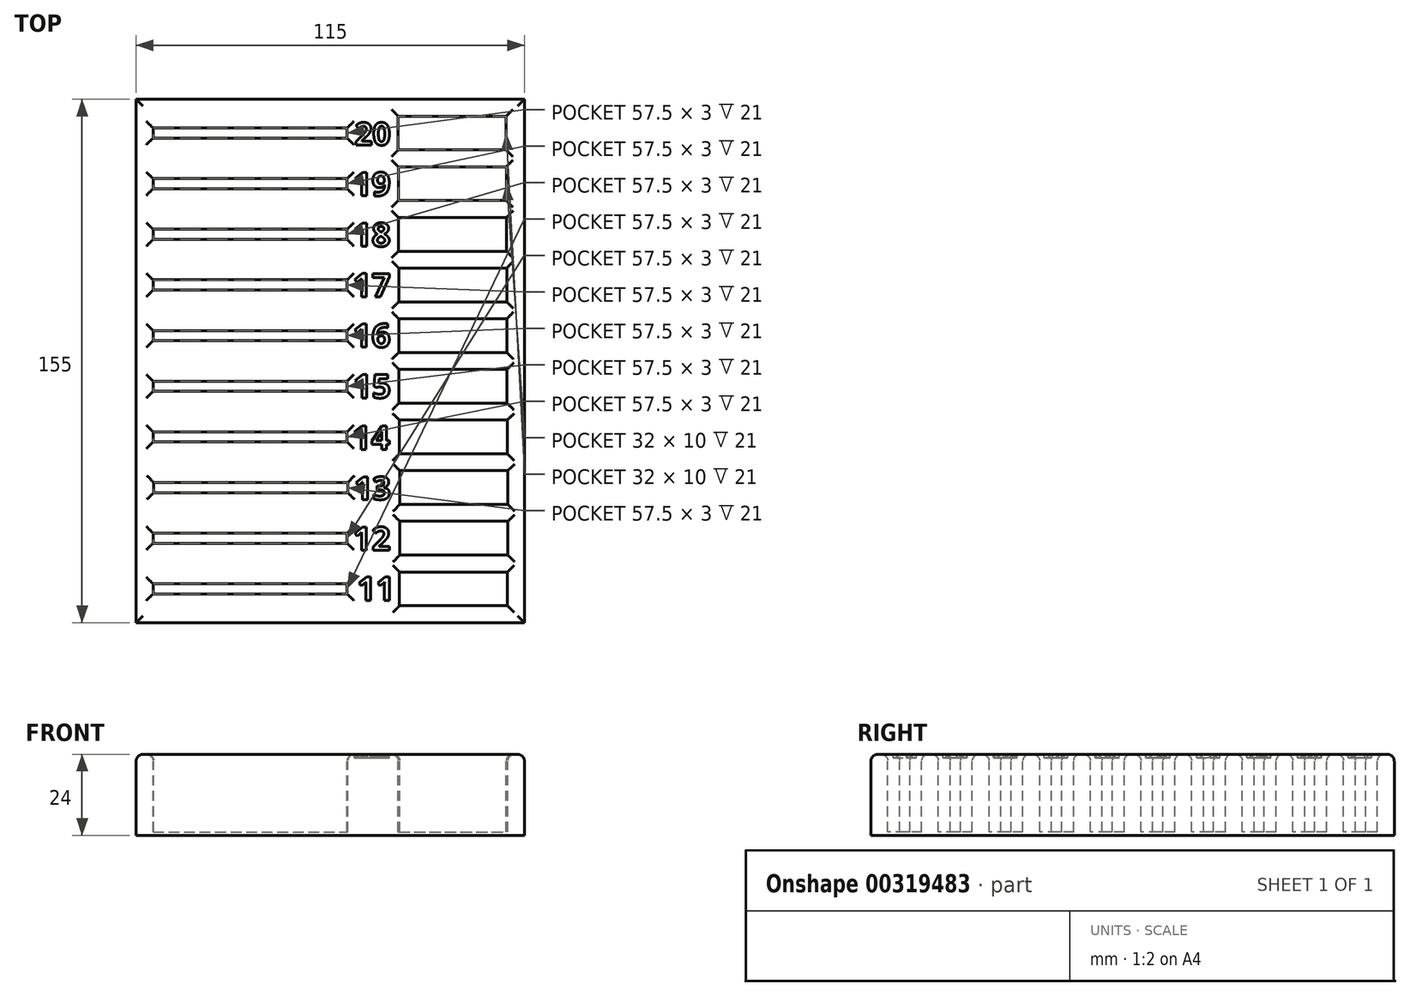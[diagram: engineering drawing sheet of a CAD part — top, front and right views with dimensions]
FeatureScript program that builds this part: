
annotation { "Feature Type Name" : "Feature", "Feature Type Description" : "" }
export const myFeature = defineFeature(function(context is Context, id is Id, definition is map)
    precondition{}
    {
        {
            var Q0;
            Q0=qCreatedBy(makeId("Top.planeOp"),FACE);
            var sketch = newSketch(context, id + "F0", { "sketchPlane" : qUnion([Q0])});
            skLineSegment(sketch, "E0.bottom", {"start": v(-49.85, 126.63) * mm, "end": v(65.15, 126.63) * mm});
            skLineSegment(sketch, "E0.top", {"start": v(-49.85, -28.37) * mm, "end": v(65.15, -28.37) * mm});
            skLineSegment(sketch, "E0.left", {"start": v(-49.85, 126.63) * mm, "end": v(-49.85, -28.37) * mm});
            skLineSegment(sketch, "E0.right", {"start": v(65.15, 126.63) * mm, "end": v(65.15, -28.37) * mm});
            skSolve(sketch);
        }
        {
            var Q0;
            Q0=makeQuery(id+"F0.imprint","IMPRINT",FACE,{"disambiguationData":[TD([[makeQuery(id+"F0.imprint","IMPRINT",EDGE,{"derivedFrom":sQuery(id+"F0.wireOp",EDGE,"E0.bottom")}),-1.0]])]});
            var Q1;
            Q1=makeQuery(id+"F0.imprint","IMPRINT",FACE,{"disambiguationData":[TD([[makeQuery(id+"F0.imprint","IMPRINT",EDGE,{"derivedFrom":sQuery(id+"F0.wireOp",EDGE,"eXpO4zti-W6eb-gkUP-Bc0d-zbJJjk6ygzeg.bottom")}),-1.0]])]});
            var Q2;
            Q2=makeQuery(id+"F0.imprint","IMPRINT",FACE,{"disambiguationData":[TD([[makeQuery(id+"F0.imprint","IMPRINT",EDGE,{"derivedFrom":sQuery(id+"F0.wireOp",EDGE,"IiJkesfC-iyIp-GpGT-9vFS-BzQ84R5pHUzr.bottom")}),-1.0]])]});
            extrude(context, id + "F1", {"entities" : qUnion([Q0, Q1, Q2]), "depth" : 24 * mm});
        }
        {
            var Q0;
            Q0=makeQuery(id+"F1.opExtrude","CAP_FACE",FACE,{"disambiguationData":[OSD([sQuery(id+"F0.wireOp",EDGE,"E0.bottom"),sQuery(id+"F0.wireOp",EDGE,"E0.top"),sQuery(id+"F0.wireOp",EDGE,"E0.left"),sQuery(id+"F0.wireOp",EDGE,"E0.right")])],"isStart":false});
            var sketch = newSketch(context, id + "F2", { "sketchPlane" : qUnion([Q0])});
            skLineSegment(sketch, "E1.bottom", {"start": v(-44.85, -16.87) * mm, "end": v(12.65, -16.87) * mm});
            skLineSegment(sketch, "E1.top", {"start": v(-44.85, -19.87) * mm, "end": v(12.65, -19.87) * mm});
            skLineSegment(sketch, "E1.left", {"start": v(-44.85, -16.87) * mm, "end": v(-44.85, -19.87) * mm});
            skLineSegment(sketch, "E1.right", {"start": v(12.65, -16.87) * mm, "end": v(12.65, -19.87) * mm});
            skLineSegment(sketch, "E2.bottom", {"start": v(28.15, -13.37) * mm, "end": v(60.15, -13.37) * mm});
            skLineSegment(sketch, "E2.top", {"start": v(28.15, -23.37) * mm, "end": v(60.15, -23.37) * mm});
            skLineSegment(sketch, "E2.left", {"start": v(28.15, -13.37) * mm, "end": v(28.15, -23.37) * mm});
            skLineSegment(sketch, "E2.right", {"start": v(60.15, -13.37) * mm, "end": v(60.15, -23.37) * mm});
            skLineSegment(sketch, "E3.bottom", {"start": v(-44.87, -1.87) * mm, "end": v(12.63, -1.87) * mm});
            skLineSegment(sketch, "E3.top", {"start": v(-44.87, -4.87) * mm, "end": v(12.63, -4.87) * mm});
            skLineSegment(sketch, "E3.left", {"start": v(-44.87, -1.87) * mm, "end": v(-44.87, -4.87) * mm});
            skLineSegment(sketch, "E3.right", {"start": v(12.63, -1.87) * mm, "end": v(12.63, -4.87) * mm});
            skLineSegment(sketch, "E4.bottom", {"start": v(28.23, 1.63) * mm, "end": v(60.23, 1.63) * mm});
            skLineSegment(sketch, "E4.top", {"start": v(28.23, -8.37) * mm, "end": v(60.23, -8.37) * mm});
            skLineSegment(sketch, "E4.left", {"start": v(28.23, 1.63) * mm, "end": v(28.23, -8.37) * mm});
            skLineSegment(sketch, "E4.right", {"start": v(60.23, 1.63) * mm, "end": v(60.23, -8.37) * mm});
            skLineSegment(sketch, "E5.bottom", {"start": v(28.24, 16.63) * mm, "end": v(60.24, 16.63) * mm});
            skLineSegment(sketch, "E5.top", {"start": v(28.24, 6.63) * mm, "end": v(60.24, 6.63) * mm});
            skLineSegment(sketch, "E5.left", {"start": v(28.24, 16.63) * mm, "end": v(28.24, 6.63) * mm});
            skLineSegment(sketch, "E5.right", {"start": v(60.24, 16.63) * mm, "end": v(60.24, 6.63) * mm});
            skLineSegment(sketch, "E6.bottom", {"start": v(28.1, 31.63) * mm, "end": v(60.1, 31.63) * mm});
            skLineSegment(sketch, "E6.top", {"start": v(28.1, 21.63) * mm, "end": v(60.1, 21.63) * mm});
            skLineSegment(sketch, "E6.left", {"start": v(28.1, 31.63) * mm, "end": v(28.1, 21.63) * mm});
            skLineSegment(sketch, "E6.right", {"start": v(60.1, 31.63) * mm, "end": v(60.1, 21.63) * mm});
            skLineSegment(sketch, "E7.bottom", {"start": v(28, 46.63) * mm, "end": v(60, 46.63) * mm});
            skLineSegment(sketch, "E7.top", {"start": v(28, 36.63) * mm, "end": v(60, 36.63) * mm});
            skLineSegment(sketch, "E7.left", {"start": v(28, 46.63) * mm, "end": v(28, 36.63) * mm});
            skLineSegment(sketch, "E7.right", {"start": v(60, 46.63) * mm, "end": v(60, 36.63) * mm});
            skLineSegment(sketch, "E8.bottom", {"start": v(27.93, 61.63) * mm, "end": v(59.93, 61.63) * mm});
            skLineSegment(sketch, "E8.top", {"start": v(27.93, 51.63) * mm, "end": v(59.93, 51.63) * mm});
            skLineSegment(sketch, "E8.left", {"start": v(27.93, 61.63) * mm, "end": v(27.93, 51.63) * mm});
            skLineSegment(sketch, "E8.right", {"start": v(59.93, 61.63) * mm, "end": v(59.93, 51.63) * mm});
            skLineSegment(sketch, "E9.bottom", {"start": v(27.91, 76.63) * mm, "end": v(59.91, 76.63) * mm});
            skLineSegment(sketch, "E9.top", {"start": v(27.91, 66.63) * mm, "end": v(59.91, 66.63) * mm});
            skLineSegment(sketch, "E9.left", {"start": v(27.91, 76.63) * mm, "end": v(27.91, 66.63) * mm});
            skLineSegment(sketch, "E9.right", {"start": v(59.91, 76.63) * mm, "end": v(59.91, 66.63) * mm});
            skLineSegment(sketch, "E10.bottom", {"start": v(27.82, 91.63) * mm, "end": v(59.82, 91.63) * mm});
            skLineSegment(sketch, "E10.top", {"start": v(27.82, 81.63) * mm, "end": v(59.82, 81.63) * mm});
            skLineSegment(sketch, "E10.left", {"start": v(27.82, 91.63) * mm, "end": v(27.82, 81.63) * mm});
            skLineSegment(sketch, "E10.right", {"start": v(59.82, 91.63) * mm, "end": v(59.82, 81.63) * mm});
            skLineSegment(sketch, "E11.bottom", {"start": v(27.78, 106.63) * mm, "end": v(59.78, 106.63) * mm});
            skLineSegment(sketch, "E11.top", {"start": v(27.78, 96.63) * mm, "end": v(59.78, 96.63) * mm});
            skLineSegment(sketch, "E11.left", {"start": v(27.78, 106.63) * mm, "end": v(27.78, 96.63) * mm});
            skLineSegment(sketch, "E11.right", {"start": v(59.78, 106.63) * mm, "end": v(59.78, 96.63) * mm});
            skLineSegment(sketch, "E12.bottom", {"start": v(27.76, 121.63) * mm, "end": v(59.76, 121.63) * mm});
            skLineSegment(sketch, "E12.top", {"start": v(27.76, 111.63) * mm, "end": v(59.76, 111.63) * mm});
            skLineSegment(sketch, "E12.left", {"start": v(27.76, 121.63) * mm, "end": v(27.76, 111.63) * mm});
            skLineSegment(sketch, "E12.right", {"start": v(59.76, 121.63) * mm, "end": v(59.76, 111.63) * mm});
            skLineSegment(sketch, "E13.bottom", {"start": v(-44.66, 13.13) * mm, "end": v(12.84, 13.13) * mm});
            skLineSegment(sketch, "E13.top", {"start": v(-44.66, 10.13) * mm, "end": v(12.84, 10.13) * mm});
            skLineSegment(sketch, "E13.left", {"start": v(-44.66, 13.13) * mm, "end": v(-44.66, 10.13) * mm});
            skLineSegment(sketch, "E13.right", {"start": v(12.84, 13.13) * mm, "end": v(12.84, 10.13) * mm});
            skLineSegment(sketch, "E14.bottom", {"start": v(-44.85, 28.13) * mm, "end": v(12.65, 28.13) * mm});
            skLineSegment(sketch, "E14.top", {"start": v(-44.85, 25.13) * mm, "end": v(12.65, 25.13) * mm});
            skLineSegment(sketch, "E14.left", {"start": v(-44.85, 28.13) * mm, "end": v(-44.85, 25.13) * mm});
            skLineSegment(sketch, "E14.right", {"start": v(12.65, 28.13) * mm, "end": v(12.65, 25.13) * mm});
            skLineSegment(sketch, "E15.bottom", {"start": v(-44.85, 43.13) * mm, "end": v(12.65, 43.13) * mm});
            skLineSegment(sketch, "E15.top", {"start": v(-44.85, 40.13) * mm, "end": v(12.65, 40.13) * mm});
            skLineSegment(sketch, "E15.left", {"start": v(-44.85, 43.13) * mm, "end": v(-44.85, 40.13) * mm});
            skLineSegment(sketch, "E15.right", {"start": v(12.65, 43.13) * mm, "end": v(12.65, 40.13) * mm});
            skLineSegment(sketch, "E16.bottom", {"start": v(-44.85, 58.13) * mm, "end": v(12.65, 58.13) * mm});
            skLineSegment(sketch, "E16.top", {"start": v(-44.85, 55.13) * mm, "end": v(12.65, 55.13) * mm});
            skLineSegment(sketch, "E16.left", {"start": v(-44.85, 58.13) * mm, "end": v(-44.85, 55.13) * mm});
            skLineSegment(sketch, "E16.right", {"start": v(12.65, 58.13) * mm, "end": v(12.65, 55.13) * mm});
            skLineSegment(sketch, "E17.bottom", {"start": v(-44.85, 73.13) * mm, "end": v(12.65, 73.13) * mm});
            skLineSegment(sketch, "E17.top", {"start": v(-44.85, 70.13) * mm, "end": v(12.65, 70.13) * mm});
            skLineSegment(sketch, "E17.left", {"start": v(-44.85, 73.13) * mm, "end": v(-44.85, 70.13) * mm});
            skLineSegment(sketch, "E17.right", {"start": v(12.65, 73.13) * mm, "end": v(12.65, 70.13) * mm});
            skLineSegment(sketch, "E18.bottom", {"start": v(-44.85, 88.13) * mm, "end": v(12.65, 88.13) * mm});
            skLineSegment(sketch, "E18.top", {"start": v(-44.85, 85.13) * mm, "end": v(12.65, 85.13) * mm});
            skLineSegment(sketch, "E18.left", {"start": v(-44.85, 88.13) * mm, "end": v(-44.85, 85.13) * mm});
            skLineSegment(sketch, "E18.right", {"start": v(12.65, 88.13) * mm, "end": v(12.65, 85.13) * mm});
            skLineSegment(sketch, "E19.bottom", {"start": v(-44.85, 103.13) * mm, "end": v(12.65, 103.13) * mm});
            skLineSegment(sketch, "E19.top", {"start": v(-44.85, 100.13) * mm, "end": v(12.65, 100.13) * mm});
            skLineSegment(sketch, "E19.left", {"start": v(-44.85, 103.13) * mm, "end": v(-44.85, 100.13) * mm});
            skLineSegment(sketch, "E19.right", {"start": v(12.65, 103.13) * mm, "end": v(12.65, 100.13) * mm});
            skLineSegment(sketch, "E20.bottom", {"start": v(-44.85, 118.13) * mm, "end": v(12.65, 118.13) * mm});
            skLineSegment(sketch, "E20.top", {"start": v(-44.85, 115.13) * mm, "end": v(12.65, 115.13) * mm});
            skLineSegment(sketch, "E20.left", {"start": v(-44.85, 118.13) * mm, "end": v(-44.85, 115.13) * mm});
            skLineSegment(sketch, "E20.right", {"start": v(12.65, 118.13) * mm, "end": v(12.65, 115.13) * mm});
            skText(sketch, "E21", { "text": "11", "fontName": "OpenSans-Bold.ttf"});
            skText(sketch, "E22", { "text": "12", "fontName": "OpenSans-Bold.ttf"});
            skText(sketch, "E23", { "text": "13", "fontName": "OpenSans-Bold.ttf"});
            skText(sketch, "E24", { "text": "14", "fontName": "OpenSans-Bold.ttf"});
            skText(sketch, "E25", { "text": "15", "fontName": "OpenSans-Bold.ttf"});
            skText(sketch, "E26", { "text": "16", "fontName": "OpenSans-Bold.ttf"});
            skText(sketch, "E27", { "text": "17", "fontName": "OpenSans-Bold.ttf"});
            skText(sketch, "E28", { "text": "18", "fontName": "OpenSans-Bold.ttf"});
            skText(sketch, "E29", { "text": "19", "fontName": "OpenSans-Bold.ttf"});
            skText(sketch, "E30", { "text": "20", "fontName": "OpenSans-Bold.ttf"});
            const initialGuessF2  = {"E21": [0.01557, -0.02179, 1, 0, 0.007], "E22": [0.01435, -0.007, 1, 0, 0.007], "E23": [0.01473, 0.00807, 1, 0, 0.0068], "E24": [0.01419, 0.02296, 1, 0, 0.007], "E25": [0.01447, 0.03817, 1, 0, 0.007], "E26": [0.01435, 0.0532, 1, 0, 0.007], "E27": [0.01435, 0.0681, 1, 0, 0.007], "E28": [0.01437, 0.08305, 1, 0, 0.007], "E29": [0.01437, 0.09806, 1, 0, 0.007], "E30": [0.01486, 0.11307, 1, 0, 0.0067]};
            skSetInitialGuess(sketch, initialGuessF2);
            skSolve(sketch);
        }
        {
            var Q0;
            Q0=makeQuery(id+"F2.imprint","IMPRINT",FACE,{"disambiguationData":[TD([[makeQuery(id+"F2.imprint","IMPRINT",EDGE,{"derivedFrom":sQuery(id+"F2.wireOp",EDGE,"E2.bottom")}),-1.0]])]});
            var Q1;
            Q1=makeQuery(id+"F2.imprint","IMPRINT",FACE,{"disambiguationData":[TD([[makeQuery(id+"F2.imprint","IMPRINT",EDGE,{"derivedFrom":sQuery(id+"F2.wireOp",EDGE,"E1.bottom")}),-1.0]])]});
            var Q2;
            Q2=makeQuery(id+"F2.imprint","IMPRINT",FACE,{"disambiguationData":[TD([[makeQuery(id+"F2.imprint","IMPRINT",EDGE,{"derivedFrom":sQuery(id+"F2.wireOp",EDGE,"E3.bottom")}),-1.0]])]});
            var Q3;
            Q3=makeQuery(id+"F2.imprint","IMPRINT",FACE,{"disambiguationData":[TD([[makeQuery(id+"F2.imprint","IMPRINT",EDGE,{"derivedFrom":sQuery(id+"F2.wireOp",EDGE,"E4.bottom")}),-1.0]])]});
            var Q4;
            Q4=makeQuery(id+"F2.imprint","IMPRINT",FACE,{"disambiguationData":[TD([[makeQuery(id+"F2.imprint","IMPRINT",EDGE,{"derivedFrom":sQuery(id+"F2.wireOp",EDGE,"E5.bottom")}),-1.0]])]});
            var Q5;
            Q5=makeQuery(id+"F2.imprint","IMPRINT",FACE,{"disambiguationData":[TD([[makeQuery(id+"F2.imprint","IMPRINT",EDGE,{"derivedFrom":sQuery(id+"F2.wireOp",EDGE,"E6.bottom")}),-1.0]])]});
            var Q6;
            Q6=makeQuery(id+"F2.imprint","IMPRINT",FACE,{"disambiguationData":[TD([[makeQuery(id+"F2.imprint","IMPRINT",EDGE,{"derivedFrom":sQuery(id+"F2.wireOp",EDGE,"E7.bottom")}),-1.0]])]});
            var Q7;
            Q7=makeQuery(id+"F2.imprint","IMPRINT",FACE,{"disambiguationData":[TD([[makeQuery(id+"F2.imprint","IMPRINT",EDGE,{"derivedFrom":sQuery(id+"F2.wireOp",EDGE,"E8.bottom")}),-1.0]])]});
            var Q8;
            Q8=makeQuery(id+"F2.imprint","IMPRINT",FACE,{"disambiguationData":[TD([[makeQuery(id+"F2.imprint","IMPRINT",EDGE,{"derivedFrom":sQuery(id+"F2.wireOp",EDGE,"E9.bottom")}),-1.0]])]});
            var Q9;
            Q9=makeQuery(id+"F2.imprint","IMPRINT",FACE,{"disambiguationData":[TD([[makeQuery(id+"F2.imprint","IMPRINT",EDGE,{"derivedFrom":sQuery(id+"F2.wireOp",EDGE,"E10.bottom")}),-1.0]])]});
            var Q10;
            Q10=makeQuery(id+"F2.imprint","IMPRINT",FACE,{"disambiguationData":[TD([[makeQuery(id+"F2.imprint","IMPRINT",EDGE,{"derivedFrom":sQuery(id+"F2.wireOp",EDGE,"E11.bottom")}),-1.0]])]});
            var Q11;
            Q11=makeQuery(id+"F2.imprint","IMPRINT",FACE,{"disambiguationData":[TD([[makeQuery(id+"F2.imprint","IMPRINT",EDGE,{"derivedFrom":sQuery(id+"F2.wireOp",EDGE,"E12.bottom")}),-1.0]])]});
            var Q12;
            Q12=makeQuery(id+"F2.imprint","IMPRINT",FACE,{"disambiguationData":[TD([[makeQuery(id+"F2.imprint","IMPRINT",EDGE,{"derivedFrom":sQuery(id+"F2.wireOp",EDGE,"E13.bottom")}),-1.0]])]});
            var Q13;
            Q13=makeQuery(id+"F2.imprint","IMPRINT",FACE,{"disambiguationData":[TD([[makeQuery(id+"F2.imprint","IMPRINT",EDGE,{"derivedFrom":sQuery(id+"F2.wireOp",EDGE,"E14.bottom")}),-1.0]])]});
            var Q14;
            Q14=makeQuery(id+"F2.imprint","IMPRINT",FACE,{"disambiguationData":[TD([[makeQuery(id+"F2.imprint","IMPRINT",EDGE,{"derivedFrom":sQuery(id+"F2.wireOp",EDGE,"E15.bottom")}),-1.0]])]});
            var Q15;
            Q15=makeQuery(id+"F2.imprint","IMPRINT",FACE,{"disambiguationData":[TD([[makeQuery(id+"F2.imprint","IMPRINT",EDGE,{"derivedFrom":sQuery(id+"F2.wireOp",EDGE,"E16.bottom")}),-1.0]])]});
            var Q16;
            Q16=makeQuery(id+"F2.imprint","IMPRINT",FACE,{"disambiguationData":[TD([[makeQuery(id+"F2.imprint","IMPRINT",EDGE,{"derivedFrom":sQuery(id+"F2.wireOp",EDGE,"E17.bottom")}),-1.0]])]});
            var Q17;
            Q17=makeQuery(id+"F2.imprint","IMPRINT",FACE,{"disambiguationData":[TD([[makeQuery(id+"F2.imprint","IMPRINT",EDGE,{"derivedFrom":sQuery(id+"F2.wireOp",EDGE,"E18.bottom")}),-1.0]])]});
            var Q18;
            Q18=makeQuery(id+"F2.imprint","IMPRINT",FACE,{"disambiguationData":[TD([[makeQuery(id+"F2.imprint","IMPRINT",EDGE,{"derivedFrom":sQuery(id+"F2.wireOp",EDGE,"E19.bottom")}),-1.0]])]});
            var Q19;
            Q19=makeQuery(id+"F2.imprint","IMPRINT",FACE,{"disambiguationData":[TD([[makeQuery(id+"F2.imprint","IMPRINT",EDGE,{"derivedFrom":sQuery(id+"F2.wireOp",EDGE,"E20.bottom")}),-1.0]])]});
            extrude(context, id + "F3", {"entities" : qUnion([Q0, Q1, Q2, Q3, Q4, Q5, Q6, Q7, Q8, Q9, Q10, Q11, Q12, Q13, Q14, Q15, Q16, Q17, Q18, Q19]), "operationType" : NewBodyOperationType.REMOVE, "oppositeDirection" : true, "depth" : 23 * mm});
        }
        {
            var Q0;
            Q0=makeQuery(id+"F3.boolean.opBoolean","COPY",EDGE,{"derivedFrom":makeQuery(id+"F3.opExtrude","CAP_EDGE",EDGE,{"disambiguationData":[OSD([sQuery(id+"F2.wireOp",EDGE,"E1.top")])],"isStart":true})});
            var Q1;
            Q1=makeQuery(id+"F3.boolean.opBoolean","COPY",EDGE,{"derivedFrom":makeQuery(id+"F3.opExtrude","CAP_EDGE",EDGE,{"disambiguationData":[OSD([sQuery(id+"F2.wireOp",EDGE,"E1.bottom")])],"isStart":true})});
            var Q2;
            Q2=makeQuery(id+"F3.boolean.opBoolean","COPY",EDGE,{"derivedFrom":makeQuery(id+"F3.opExtrude","CAP_EDGE",EDGE,{"disambiguationData":[OSD([sQuery(id+"F2.wireOp",EDGE,"E1.right")])],"isStart":true})});
            var Q3;
            Q3=makeQuery(id+"F3.boolean.opBoolean","COPY",EDGE,{"derivedFrom":makeQuery(id+"F3.opExtrude","CAP_EDGE",EDGE,{"disambiguationData":[OSD([sQuery(id+"F2.wireOp",EDGE,"E1.left")])],"isStart":true})});
            var Q4;
            Q4=makeQuery(id+"F3.boolean.opBoolean","COPY",EDGE,{"derivedFrom":makeQuery(id+"F3.opExtrude","CAP_EDGE",EDGE,{"disambiguationData":[OSD([sQuery(id+"F2.wireOp",EDGE,"E2.bottom")])],"isStart":true})});
            var Q5;
            Q5=makeQuery(id+"F3.boolean.opBoolean","COPY",EDGE,{"derivedFrom":makeQuery(id+"F3.opExtrude","CAP_EDGE",EDGE,{"disambiguationData":[OSD([sQuery(id+"F2.wireOp",EDGE,"E2.top")])],"isStart":true})});
            var Q6;
            Q6=makeQuery(id+"F3.boolean.opBoolean","COPY",EDGE,{"derivedFrom":makeQuery(id+"F3.opExtrude","CAP_EDGE",EDGE,{"disambiguationData":[OSD([sQuery(id+"F2.wireOp",EDGE,"E2.left")])],"isStart":true})});
            var Q7;
            Q7=makeQuery(id+"F3.boolean.opBoolean","COPY",EDGE,{"derivedFrom":makeQuery(id+"F3.opExtrude","CAP_EDGE",EDGE,{"disambiguationData":[OSD([sQuery(id+"F2.wireOp",EDGE,"E2.right")])],"isStart":true})});
            var Q8;
            Q8=makeQuery(id+"F3.boolean.opBoolean","COPY",EDGE,{"derivedFrom":makeQuery(id+"F3.opExtrude","CAP_EDGE",EDGE,{"disambiguationData":[OSD([sQuery(id+"F2.wireOp",EDGE,"E3.bottom")])],"isStart":true})});
            var Q9;
            Q9=makeQuery(id+"F3.boolean.opBoolean","COPY",EDGE,{"derivedFrom":makeQuery(id+"F3.opExtrude","CAP_EDGE",EDGE,{"disambiguationData":[OSD([sQuery(id+"F2.wireOp",EDGE,"E3.top")])],"isStart":true})});
            var Q10;
            Q10=makeQuery(id+"F3.boolean.opBoolean","COPY",EDGE,{"derivedFrom":makeQuery(id+"F3.opExtrude","CAP_EDGE",EDGE,{"disambiguationData":[OSD([sQuery(id+"F2.wireOp",EDGE,"E3.left")])],"isStart":true})});
            var Q11;
            Q11=makeQuery(id+"F3.boolean.opBoolean","COPY",EDGE,{"derivedFrom":makeQuery(id+"F3.opExtrude","CAP_EDGE",EDGE,{"disambiguationData":[OSD([sQuery(id+"F2.wireOp",EDGE,"E3.right")])],"isStart":true})});
            var Q12;
            Q12=makeQuery(id+"F3.boolean.opBoolean","COPY",EDGE,{"derivedFrom":makeQuery(id+"F3.opExtrude","CAP_EDGE",EDGE,{"disambiguationData":[OSD([sQuery(id+"F2.wireOp",EDGE,"E4.left")])],"isStart":true})});
            var Q13;
            Q13=makeQuery(id+"F3.boolean.opBoolean","COPY",EDGE,{"derivedFrom":makeQuery(id+"F3.opExtrude","CAP_EDGE",EDGE,{"disambiguationData":[OSD([sQuery(id+"F2.wireOp",EDGE,"E4.bottom")])],"isStart":true})});
            var Q14;
            Q14=makeQuery(id+"F3.boolean.opBoolean","COPY",EDGE,{"derivedFrom":makeQuery(id+"F3.opExtrude","CAP_EDGE",EDGE,{"disambiguationData":[OSD([sQuery(id+"F2.wireOp",EDGE,"E4.right")])],"isStart":true})});
            var Q15;
            Q15=makeQuery(id+"F3.boolean.opBoolean","COPY",EDGE,{"derivedFrom":makeQuery(id+"F3.opExtrude","CAP_EDGE",EDGE,{"disambiguationData":[OSD([sQuery(id+"F2.wireOp",EDGE,"E4.top")])],"isStart":true})});
            var Q16;
            Q16=makeQuery(id+"F3.boolean.opBoolean","COPY",EDGE,{"derivedFrom":makeQuery(id+"F3.opExtrude","CAP_EDGE",EDGE,{"disambiguationData":[OSD([sQuery(id+"F2.wireOp",EDGE,"E5.top")])],"isStart":true})});
            var Q17;
            Q17=makeQuery(id+"F3.boolean.opBoolean","COPY",EDGE,{"derivedFrom":makeQuery(id+"F3.opExtrude","CAP_EDGE",EDGE,{"disambiguationData":[OSD([sQuery(id+"F2.wireOp",EDGE,"E5.left")])],"isStart":true})});
            var Q18;
            Q18=makeQuery(id+"F3.boolean.opBoolean","COPY",EDGE,{"derivedFrom":makeQuery(id+"F3.opExtrude","CAP_EDGE",EDGE,{"disambiguationData":[OSD([sQuery(id+"F2.wireOp",EDGE,"E5.bottom")])],"isStart":true})});
            var Q19;
            Q19=makeQuery(id+"F3.boolean.opBoolean","COPY",EDGE,{"derivedFrom":makeQuery(id+"F3.opExtrude","CAP_EDGE",EDGE,{"disambiguationData":[OSD([sQuery(id+"F2.wireOp",EDGE,"E5.right")])],"isStart":true})});
            var Q20;
            Q20=makeQuery(id+"F3.boolean.opBoolean","COPY",EDGE,{"derivedFrom":makeQuery(id+"F3.opExtrude","CAP_EDGE",EDGE,{"disambiguationData":[OSD([sQuery(id+"F2.wireOp",EDGE,"E6.top")])],"isStart":true})});
            var Q21;
            Q21=makeQuery(id+"F3.boolean.opBoolean","COPY",EDGE,{"derivedFrom":makeQuery(id+"F3.opExtrude","CAP_EDGE",EDGE,{"disambiguationData":[OSD([sQuery(id+"F2.wireOp",EDGE,"E6.right")])],"isStart":true})});
            var Q22;
            Q22=makeQuery(id+"F3.boolean.opBoolean","COPY",EDGE,{"derivedFrom":makeQuery(id+"F3.opExtrude","CAP_EDGE",EDGE,{"disambiguationData":[OSD([sQuery(id+"F2.wireOp",EDGE,"E6.bottom")])],"isStart":true})});
            var Q23;
            Q23=makeQuery(id+"F3.boolean.opBoolean","COPY",EDGE,{"derivedFrom":makeQuery(id+"F3.opExtrude","CAP_EDGE",EDGE,{"disambiguationData":[OSD([sQuery(id+"F2.wireOp",EDGE,"E6.left")])],"isStart":true})});
            var Q24;
            Q24=makeQuery(id+"F3.boolean.opBoolean","COPY",EDGE,{"derivedFrom":makeQuery(id+"F3.opExtrude","CAP_EDGE",EDGE,{"disambiguationData":[OSD([sQuery(id+"F2.wireOp",EDGE,"E7.left")])],"isStart":true})});
            var Q25;
            Q25=makeQuery(id+"F3.boolean.opBoolean","COPY",EDGE,{"derivedFrom":makeQuery(id+"F3.opExtrude","CAP_EDGE",EDGE,{"disambiguationData":[OSD([sQuery(id+"F2.wireOp",EDGE,"E7.bottom")])],"isStart":true})});
            var Q26;
            Q26=makeQuery(id+"F1.opExtrude","CAP_FACE",FACE,{"disambiguationData":[OSD([sQuery(id+"F0.wireOp",EDGE,"E0.bottom"),sQuery(id+"F0.wireOp",EDGE,"E0.top"),sQuery(id+"F0.wireOp",EDGE,"E0.left"),sQuery(id+"F0.wireOp",EDGE,"E0.right")])],"isStart":false});
            var Q27;
            Q27=makeQuery(id+"F3.boolean.opBoolean","COPY",EDGE,{"derivedFrom":makeQuery(id+"F3.opExtrude","CAP_EDGE",EDGE,{"disambiguationData":[OSD([sQuery(id+"F2.wireOp",EDGE,"E7.right")])],"isStart":true})});
            fillet(context, id + "F4", {"entities" : qUnion([Q0, Q1, Q2, Q3, Q4, Q5, Q6, Q7, Q8, Q9, Q10, Q11, Q12, Q13, Q14, Q15, Q16, Q17, Q18, Q19, Q20, Q21, Q22, Q23, Q24, Q25, Q26, Q27]), "radius" : 2 * mm, "tangentPropagation" : true, "allowEdgeOverflow" : false});
        }
        {
            var Q0;
            Q0=makeQuery(id+"F2.imprint","IMPRINT",FACE,{"disambiguationData":[TD([[makeQuery(id+"F2.imprint","IMPRINT",EDGE,{"derivedFrom":sQuery(id+"F2.wireOp",EDGE,"E21.sketch_text.stroke-0")}),-1.0]])]});
            var Q1;
            Q1=makeQuery(id+"F2.imprint","IMPRINT",FACE,{"disambiguationData":[TD([[makeQuery(id+"F2.imprint","IMPRINT",EDGE,{"derivedFrom":sQuery(id+"F2.wireOp",EDGE,"E21.sketch_text.stroke-9")}),-1.0]])]});
            var Q2;
            Q2=makeQuery(id+"F2.imprint","IMPRINT",FACE,{"disambiguationData":[TD([[makeQuery(id+"F2.imprint","IMPRINT",EDGE,{"derivedFrom":sQuery(id+"F2.wireOp",EDGE,"E22.sketch_text.stroke-10")}),-1.0]])]});
            var Q3;
            Q3=makeQuery(id+"F2.imprint","IMPRINT",FACE,{"disambiguationData":[TD([[makeQuery(id+"F2.imprint","IMPRINT",EDGE,{"derivedFrom":sQuery(id+"F2.wireOp",EDGE,"E22.sketch_text.stroke-0")}),-1.0]])]});
            var Q4;
            Q4=makeQuery(id+"F2.imprint","IMPRINT",FACE,{"disambiguationData":[TD([[makeQuery(id+"F2.imprint","IMPRINT",EDGE,{"derivedFrom":sQuery(id+"F2.wireOp",EDGE,"E23.sketch_text.stroke-0")}),-1.0]])]});
            var Q5;
            Q5=makeQuery(id+"F2.imprint","IMPRINT",FACE,{"disambiguationData":[TD([[makeQuery(id+"F2.imprint","IMPRINT",EDGE,{"derivedFrom":sQuery(id+"F2.wireOp",EDGE,"E23.sketch_text.stroke-10")}),-1.0]])]});
            var Q6;
            Q6=makeQuery(id+"F2.imprint","IMPRINT",FACE,{"disambiguationData":[TD([[makeQuery(id+"F2.imprint","IMPRINT",EDGE,{"derivedFrom":sQuery(id+"F2.wireOp",EDGE,"E24.sketch_text.stroke-0")}),-1.0]])]});
            var Q7;
            Q7=makeQuery(id+"F2.imprint","IMPRINT",FACE,{"disambiguationData":[TD([[makeQuery(id+"F2.imprint","IMPRINT",EDGE,{"derivedFrom":sQuery(id+"F2.wireOp",EDGE,"E24.sketch_text.stroke-10")}),-1.0]])]});
            var Q8;
            Q8=makeQuery(id+"F2.imprint","IMPRINT",FACE,{"disambiguationData":[TD([[makeQuery(id+"F2.imprint","IMPRINT",EDGE,{"derivedFrom":sQuery(id+"F2.wireOp",EDGE,"E25.sketch_text.stroke-10")}),-1.0]])]});
            var Q9;
            Q9=makeQuery(id+"F2.imprint","IMPRINT",FACE,{"disambiguationData":[TD([[makeQuery(id+"F2.imprint","IMPRINT",EDGE,{"derivedFrom":sQuery(id+"F2.wireOp",EDGE,"E25.sketch_text.stroke-0")}),-1.0]])]});
            var Q10;
            Q10=makeQuery(id+"F2.imprint","IMPRINT",FACE,{"disambiguationData":[TD([[makeQuery(id+"F2.imprint","IMPRINT",EDGE,{"derivedFrom":sQuery(id+"F2.wireOp",EDGE,"E26.sketch_text.stroke-10")}),-1.0]])]});
            var Q11;
            Q11=makeQuery(id+"F2.imprint","IMPRINT",FACE,{"disambiguationData":[TD([[makeQuery(id+"F2.imprint","IMPRINT",EDGE,{"derivedFrom":sQuery(id+"F2.wireOp",EDGE,"E26.sketch_text.stroke-0")}),-1.0]])]});
            var Q12;
            Q12=makeQuery(id+"F2.imprint","IMPRINT",FACE,{"disambiguationData":[TD([[makeQuery(id+"F2.imprint","IMPRINT",EDGE,{"derivedFrom":sQuery(id+"F2.wireOp",EDGE,"E27.sketch_text.stroke-10")}),-1.0]])]});
            var Q13;
            Q13=makeQuery(id+"F2.imprint","IMPRINT",FACE,{"disambiguationData":[TD([[makeQuery(id+"F2.imprint","IMPRINT",EDGE,{"derivedFrom":sQuery(id+"F2.wireOp",EDGE,"E27.sketch_text.stroke-0")}),-1.0]])]});
            var Q14;
            Q14=makeQuery(id+"F2.imprint","IMPRINT",FACE,{"disambiguationData":[TD([[makeQuery(id+"F2.imprint","IMPRINT",EDGE,{"derivedFrom":sQuery(id+"F2.wireOp",EDGE,"E28.sketch_text.stroke-10")}),-1.0]])]});
            var Q15;
            Q15=makeQuery(id+"F2.imprint","IMPRINT",FACE,{"disambiguationData":[TD([[makeQuery(id+"F2.imprint","IMPRINT",EDGE,{"derivedFrom":sQuery(id+"F2.wireOp",EDGE,"E28.sketch_text.stroke-0")}),-1.0]])]});
            var Q16;
            Q16=makeQuery(id+"F2.imprint","IMPRINT",FACE,{"disambiguationData":[TD([[makeQuery(id+"F2.imprint","IMPRINT",EDGE,{"derivedFrom":sQuery(id+"F2.wireOp",EDGE,"E29.sketch_text.stroke-10")}),-1.0]])]});
            var Q17;
            Q17=makeQuery(id+"F2.imprint","IMPRINT",FACE,{"disambiguationData":[TD([[makeQuery(id+"F2.imprint","IMPRINT",EDGE,{"derivedFrom":sQuery(id+"F2.wireOp",EDGE,"E29.sketch_text.stroke-0")}),-1.0]])]});
            var Q18;
            Q18=makeQuery(id+"F2.imprint","IMPRINT",FACE,{"disambiguationData":[TD([[makeQuery(id+"F2.imprint","IMPRINT",EDGE,{"derivedFrom":sQuery(id+"F2.wireOp",EDGE,"E30.sketch_text.stroke-24")}),-1.0]])]});
            var Q19;
            Q19=makeQuery(id+"F2.imprint","IMPRINT",FACE,{"disambiguationData":[TD([[makeQuery(id+"F2.imprint","IMPRINT",EDGE,{"derivedFrom":sQuery(id+"F2.wireOp",EDGE,"E30.sketch_text.stroke-0")}),-1.0]])]});
            var Q20;
            Q20=makeQuery(id+"F2.imprint","IMPRINT",FACE,{"disambiguationData":[TD([[makeQuery(id+"F2.imprint","IMPRINT",EDGE,{"derivedFrom":sQuery(id+"F2.wireOp",EDGE,"E21.sketch_text.stroke-10")}),-1.0]])]});
            extrude(context, id + "F5", {"entities" : qUnion([Q0, Q1, Q2, Q3, Q4, Q5, Q6, Q7, Q8, Q9, Q10, Q11, Q12, Q13, Q14, Q15, Q16, Q17, Q18, Q19, Q20]), "operationType" : NewBodyOperationType.REMOVE, "oppositeDirection" : true, "depth" : 1 * mm});
        }
    });
